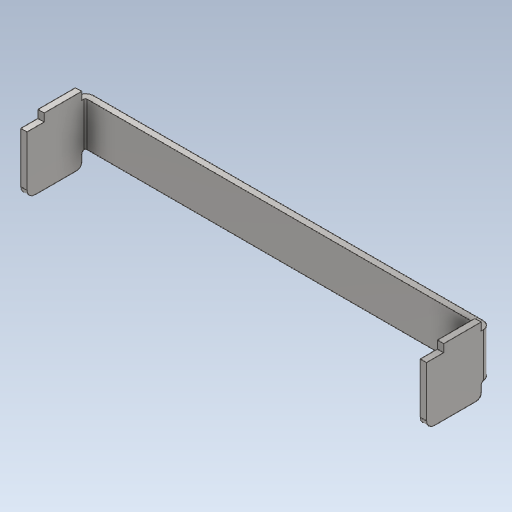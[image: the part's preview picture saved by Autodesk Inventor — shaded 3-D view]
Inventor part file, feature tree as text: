
AUTODESK INVENTOR PART (.ipt)
format: ipt  version: 2020 (Build 240168000, 168)  size: 290,816 bytes
history: native  units: mm
features: other x4, extrude x1
ambient origin geometry x8: Origin, YZ Plane, XZ Plane, XY Plane, X Axis, Y Axis, Z Axis, Center Point
bodies: Body1 (feature_tree)
feature tree (5):
  other  "實體1"
  extrude  "擠出1"  Depth=2.0mm TaperAngle=0.0deg
  other  "折彎零件1"
  other  "折彎零件2"
  other  "定義1"
